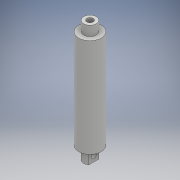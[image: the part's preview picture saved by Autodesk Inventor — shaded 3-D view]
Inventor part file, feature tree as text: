
AUTODESK INVENTOR PART (.ipt)
format: ipt  version: 2017 (Build 210142000, 142)  size: 130,560 bytes
history: native  units: mm
features: extrude x6, sketch x6
ambient origin geometry x8: Origin, YZ Plane, XZ Plane, XY Plane, X Axis, Y Axis, Z Axis, Center Point
bodies: Solid1 (feature_tree)
feature tree (12):
  extrude  "Extrusion1"  Depth=125.0mm TaperAngle=0.0deg
  extrude  "Extrusion2"  Depth=12.5mm TaperAngle=0.0deg
  extrude  "Extrusion3"  Depth=50.8mm TaperAngle=0.0deg
  extrude  "Extrusion4"  Depth=16.0mm TaperAngle=0.0deg
  extrude  "Extrusion5"  Depth=16.0mm TaperAngle=0.0deg
  extrude  "Extrusion6"  Depth=16.0mm
  sketch  "Sketch1"  dims[d0=28.5mm d1=125.0mm d2=0.0mm]
  sketch  "Sketch2"  dims[d3=15.875mm d4=12.5mm d5=0.0mm]
  sketch  "Sketch3"  dims[d6=8.0mm d7=50.8mm d8=0.0mm]
  sketch  "Sketch4"  dims[d9=15.875mm d10=16.0mm d11=0.0mm]
  sketch  "Sketch5"  dims[d12=9.5mm d13=16.0mm d14=0.0mm]
  sketch  "Sketch6"  dims[d15=6.4mm d16=7.0mm d17=16.0mm d18=0.0mm]
